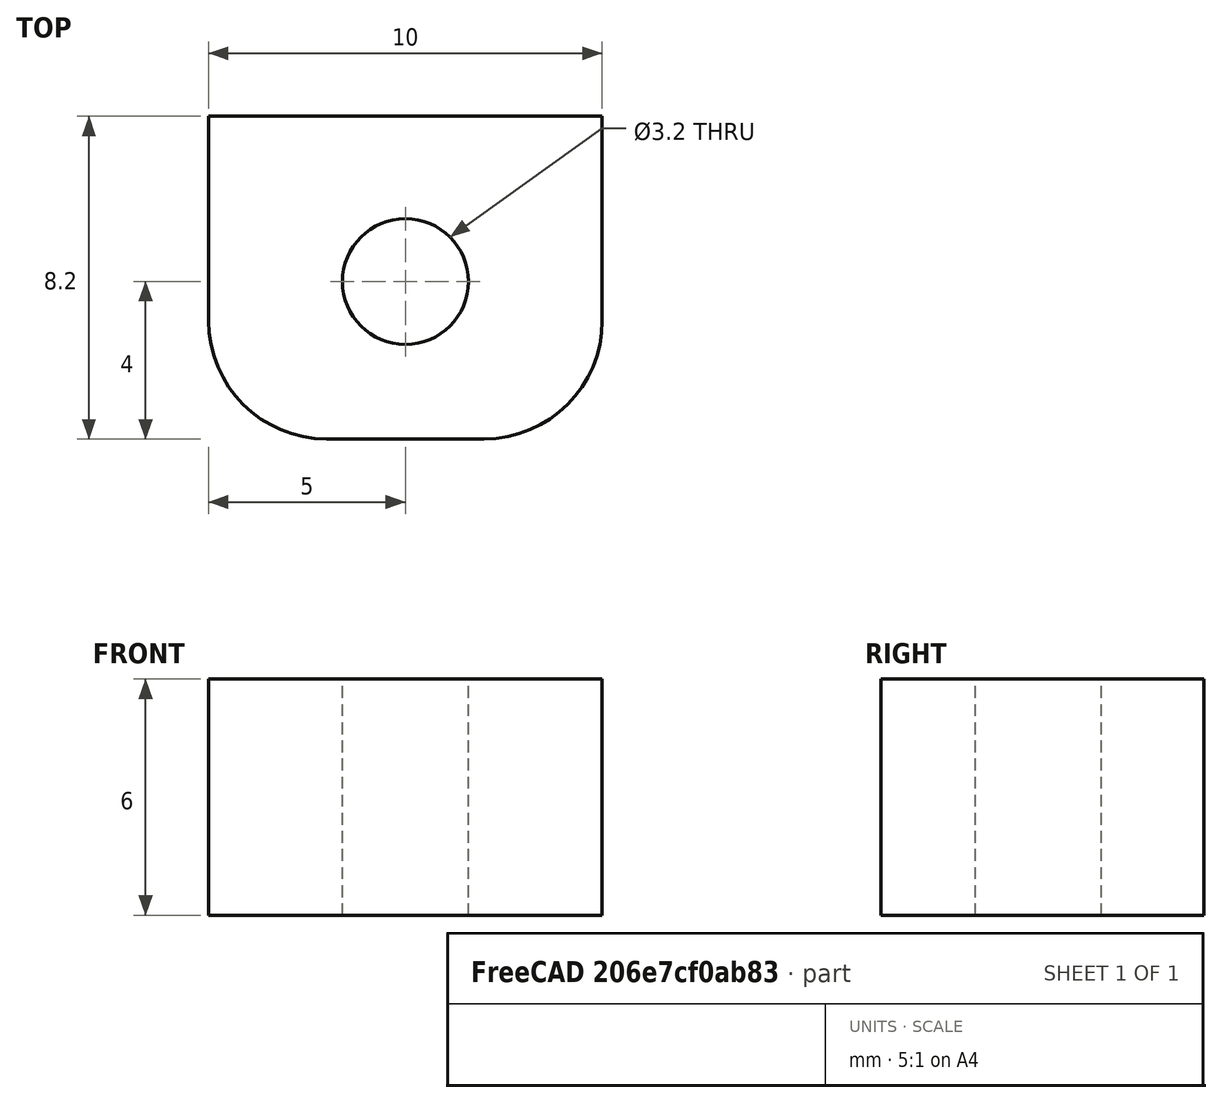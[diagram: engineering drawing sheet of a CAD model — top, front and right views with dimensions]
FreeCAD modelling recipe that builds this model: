
FCSTD DOCUMENT  (FreeCAD 0.18R14090 (Git))
Label: CarriageBeltClamp
License: All rights reserved
LicenseURL: http://en.wikipedia.org/wiki/All_rights_reserved
objects: Part::Box×1, Part::Cylinder×1, Part::Cut×1, Part::Fillet×1, App::Part×1
note: 4 computed .brp shape members not serialized (recipe doc carries the construction recipe); baked Part::Feature solids carry a one-line shape summary decoded from their .brp

FEATURE [Part::Box] Box  label="ClampCube"
  AttacherType = Attacher::AttachEngine3D
  Height = 6
  Length = 10
  Width = 8.2
FEATURE [Part::Cylinder] Cylinder  label="ClampCilinder"
  Angle = 360
  AttacherType = Attacher::AttachEngine3D
  Height = 6
  Placement = pos=(5,4,0) rot=(0,0,1;0rad)
  Radius = 1.6
FEATURE [Part::Cut] Cut  label="ClampCut"
  Base = -> Box
  Tool = -> Cylinder
FEATURE [Part::Fillet] Fillet  label="ClampFillet"
  Base = -> Cut
  Edges = 2 edges r=3: [Edge1,Edge6]
FEATURE [App::Part] Part  label="ClampPart"
  Group = -> [Cut,Box,Cylinder,Fillet]
  License = CC BY 3.0
  LicenseURL = http://creativecommons.org/licenses/by/3.0/
  Origin = -> Origin
